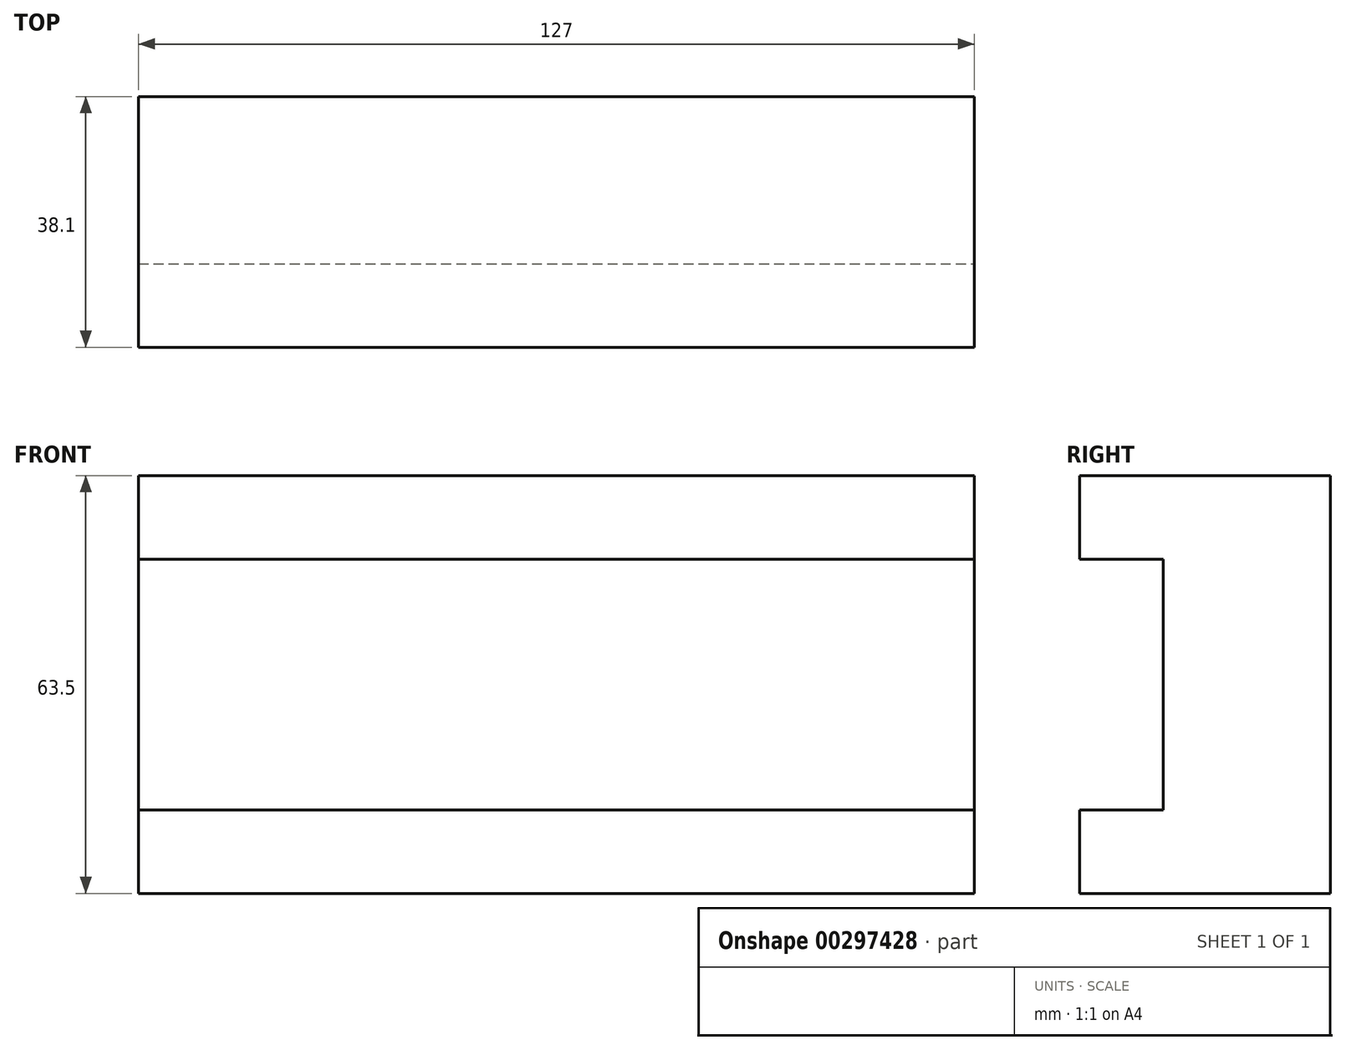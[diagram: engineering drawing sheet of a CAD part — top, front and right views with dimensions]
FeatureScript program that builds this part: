
annotation { "Feature Type Name" : "Feature", "Feature Type Description" : "" }
export const myFeature = defineFeature(function(context is Context, id is Id, definition is map)
    precondition{}
    {
        {
            var Q0;
            Q0=qCreatedBy(makeId("Front.planeOp"),FACE);
            var sketch = newSketch(context, id + "F0", { "sketchPlane" : qUnion([Q0])});
            skLineSegment(sketch, "E0.bottom", {"start": v(63.5, 31.75) * mm, "end": v(-63.5, 31.75) * mm});
            skLineSegment(sketch, "E0.top", {"start": v(63.5, -31.75) * mm, "end": v(-63.5, -31.75) * mm});
            skLineSegment(sketch, "E0.left", {"start": v(63.5, 31.75) * mm, "end": v(63.5, -31.75) * mm});
            skLineSegment(sketch, "E0.right", {"start": v(-63.5, 31.75) * mm, "end": v(-63.5, -31.75) * mm});
            skPoint(sketch, "E0.middle", {"position": v(0, 0) * mm});
            skSolve(sketch);
        }
        {
            var Q0;
            Q0 = qSketchRegion(id + "F0", true);
            extrude(context, id + "F1", {"entities" : qUnion([Q0]), "depth" : 25.4 * mm});
        }
        {
            var Q0;
            Q0=makeQuery(id+"F1.opExtrude","CAP_FACE",FACE,{"disambiguationData":[OSD([sQuery(id+"F0.wireOp",EDGE,"E0.bottom"),sQuery(id+"F0.wireOp",EDGE,"E0.top"),sQuery(id+"F0.wireOp",EDGE,"E0.left"),sQuery(id+"F0.wireOp",EDGE,"E0.right")])],"isStart":false});
            var sketch = newSketch(context, id + "F2", { "sketchPlane" : qUnion([Q0])});
            skLineSegment(sketch, "E1.bottom", {"start": v(-63.5, 31.75) * mm, "end": v(63.5, 31.75) * mm});
            skLineSegment(sketch, "E1.top", {"start": v(-63.5, 19.05) * mm, "end": v(63.5, 19.05) * mm});
            skLineSegment(sketch, "E1.left", {"start": v(-63.5, 31.75) * mm, "end": v(-63.5, 19.05) * mm});
            skLineSegment(sketch, "E1.right", {"start": v(63.5, 31.75) * mm, "end": v(63.5, 19.05) * mm});
            skLineSegment(sketch, "E2.bottom", {"start": v(-63.5, -31.75) * mm, "end": v(63.5, -31.75) * mm});
            skLineSegment(sketch, "E2.top", {"start": v(-63.5, -19.05) * mm, "end": v(63.5, -19.05) * mm});
            skLineSegment(sketch, "E2.left", {"start": v(-63.5, -31.75) * mm, "end": v(-63.5, -19.05) * mm});
            skLineSegment(sketch, "E2.right", {"start": v(63.5, -31.75) * mm, "end": v(63.5, -19.05) * mm});
            skSolve(sketch);
        }
        {
            var Q0;
            Q0 = qSketchRegion(id + "F2", true);
            extrude(context, id + "F3", {"entities" : qUnion([Q0]), "operationType" : NewBodyOperationType.ADD, "depth" : 12.7 * mm});
        }
    });
